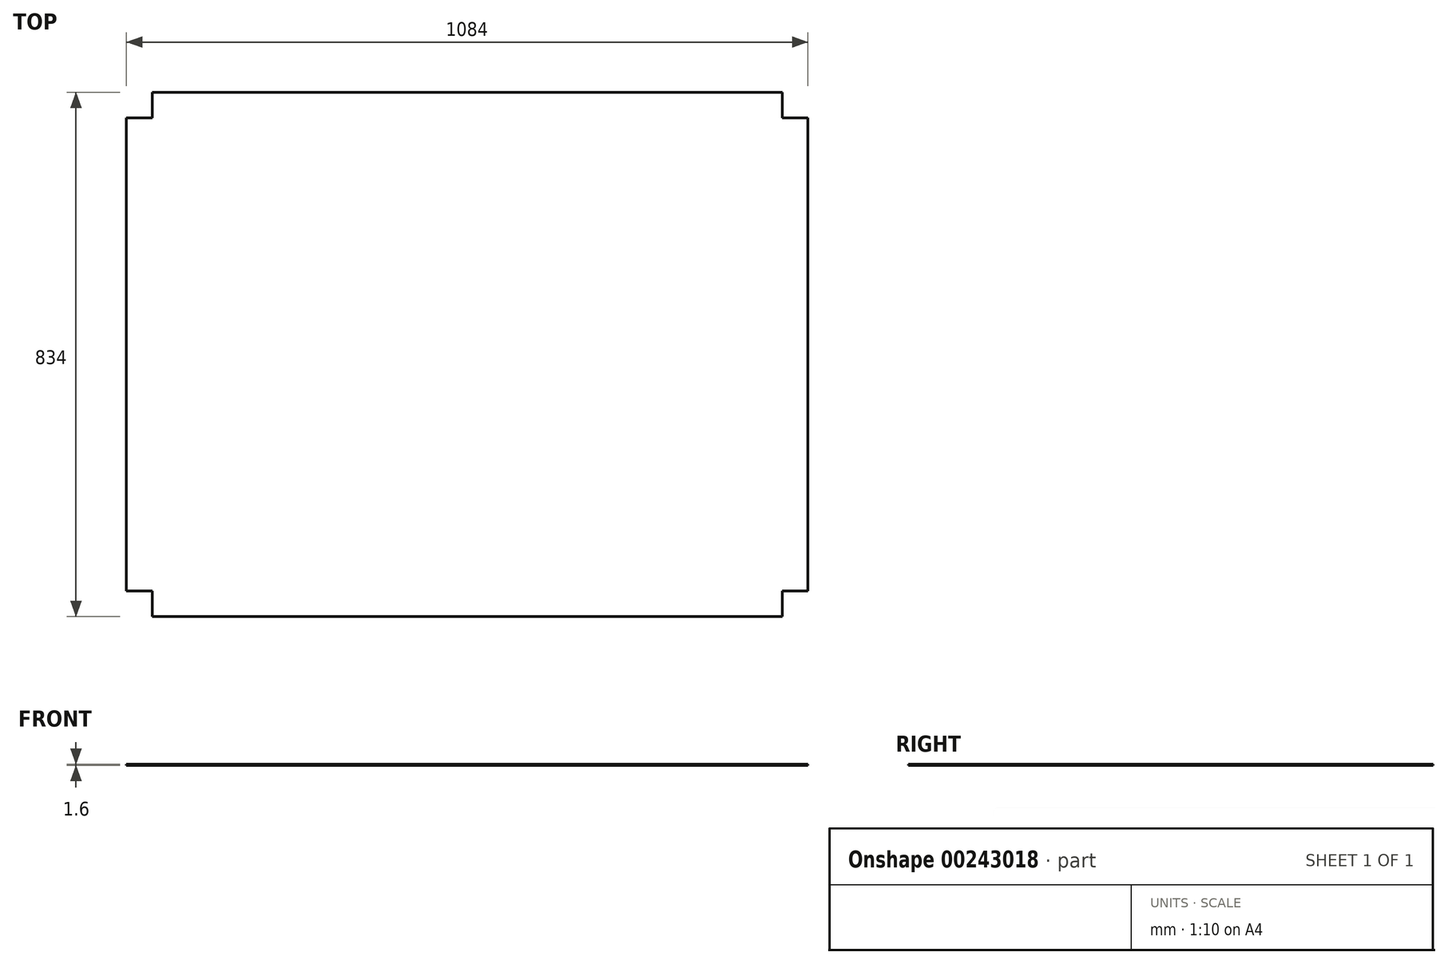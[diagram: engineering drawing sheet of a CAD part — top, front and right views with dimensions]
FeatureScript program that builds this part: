
annotation { "Feature Type Name" : "Feature", "Feature Type Description" : "" }
export const myFeature = defineFeature(function(context is Context, id is Id, definition is map)
    precondition{}
    {
        {
            var Q0;
            Q0=qCreatedBy(makeId("Top.planeOp"),FACE);
            var sketch = newSketch(context, id + "F0", { "sketchPlane" : qUnion([Q0])});
            skLineSegment(sketch, "E0.bottom", {"start": v(501, 417) * mm, "end": v(-501, 417) * mm});
            skLineSegment(sketch, "E0.top", {"start": v(501, -417) * mm, "end": v(-501, -417) * mm});
            skLineSegment(sketch, "E0.left", {"start": v(542, 376) * mm, "end": v(542, -376) * mm});
            skLineSegment(sketch, "E0.right", {"start": v(-542, 376) * mm, "end": v(-542, -376) * mm});
            skPoint(sketch, "E0.middle", {"position": v(0, 0) * mm});
            skLineSegment(sketch, "E1.top", {"start": v(-542, 376) * mm, "end": v(-501, 376) * mm});
            skLineSegment(sketch, "E1.right", {"start": v(-501, 417) * mm, "end": v(-501, 376) * mm});
            skLineSegment(sketch, "E2.top", {"start": v(542, 376) * mm, "end": v(501, 376) * mm});
            skLineSegment(sketch, "E2.right", {"start": v(501, 417) * mm, "end": v(501, 376) * mm});
            skLineSegment(sketch, "E3.top", {"start": v(542, -376) * mm, "end": v(501, -376) * mm});
            skLineSegment(sketch, "E3.right", {"start": v(501, -417) * mm, "end": v(501, -376) * mm});
            skLineSegment(sketch, "E4.top", {"start": v(-542, -376) * mm, "end": v(-501, -376) * mm});
            skLineSegment(sketch, "E4.right", {"start": v(-501, -417) * mm, "end": v(-501, -376) * mm});
            skPoint(sketch, "E5.orphan", {"position": v(-542, 417) * mm});
            skPoint(sketch, "E6.orphan", {"position": v(542, 417) * mm});
            skPoint(sketch, "E7.orphan", {"position": v(542, -417) * mm});
            skPoint(sketch, "E8.orphan", {"position": v(-542, -417) * mm});
            skSolve(sketch);
        }
        {
            var Q0;
            Q0 = qSketchRegion(id + "F0", true);
            extrude(context, id + "F1", {"entities" : qUnion([Q0]), "depth" : 1.6 * mm});
        }
    });
